# Revit family: QF_ELECTROLUXPROFESSIONAL_1LSNTN_WN6-20_E
name_source: partatom
category: Attrezzature speciali
units: mm (PartAtom-declared; Revit-internal decimal feet)

## family parameters
Basato su piano di lavoro = No
Condiviso = No
Punto di calcolo locali = No
Quota connettore circolare = Usa diametro
Sempre verticale = Sì
Taglio con vuoti quando caricato = No
Tipo di parte = Normale

## types (37) — shared parameters
Depth = 915.5 mm  [stored 3.00361 ft]
Depth Actual = 915 mm  [stored 3.00197 ft]
Height = 1346.8 mm  [stored 4.41864 ft]
Height Actual = 1345 mm
Latent Heat Output = 0.0
Length Actual = 750 mm  [stored 2.46063 ft]
Modello = WN6-20
Produttore = Electrolux Professional
Sensible Heat Output = 0.0
URL = www.electroluxprofessional.com
Weight = 207
Width = 750 mm  [stored 2.46063 ft]
zero-valued in all types: Gas KW, Prospetto di default, Steam Pounds per Hour

## per-type parameters (varying)
| type | Cycle | Descrizione | Item Number | Phase | Volts | Watts |
| 9867830144 | 50 Hz | WASHER WN6-20 20KG NO HEAT 220-240/50/1N COMPASS PRO 6G01 ML 2xWATER POWDER+5xLIQ. VALV.OPEN SILVER 2.I/O DISCON. STOP | 1L0GCA | 1 | 240 V | 800 W |
| 9867830154 | 50 Hz | WASHER WN6-20 20KG EL 13KW 220-240/50/3 COMPASS PRO 6G01 ML 2xWATER POWDER+5xLIQ. VALV.OPEN SILVER 2.I/O DISCON. STOP | 1LSP91 | 3 | 240 V | 13500 W |
| 9867830253 | 50 Hz | WASHER WN6-20 20KG NO HEAT 220-240/50/1N COMPASS PRO 6G01 ML 2xWATER POWDER VALV.OPEN SILVER DISCON. STOP | 1LSPS4 | 1 | 240 V | 800 W |
| 9867830293 | 50 Hz | WASHER WN6-20 20KG EL 13KW 380-415/50/3 COMPASS PRO 6G07 ML 2xWATER POWDER+5xLIQ. VALV.OPEN SILVER 2.I/O TRAFO DISCON. S | 1LT6KV | 3 | 415 V | 13500 W |
| 9867830266 | 60 Hz | WASHER WN6-20 20KG NO HEAT 220-240/60/1N COMPASS PRO 6L01 ML 2xWATER POWDER+5xLIQ. VALV.OPEN SILVER 2.I/O DISCON. | 1L0H63 | 1 | 240 V | 800 W |
| 9867830286 | 60 Hz | WASHER WN6-20 20KG EL 13KW 440/60/3 COMPASS PRO 6H01 ML 2xWATER POWDER+5xLIQ. VALV.OPEN SST/SILVER 2.I/O TRAFO DISCON. S | 1LM0CL | 3 | 440 V | 13700 W |
| 9867830141 | 50 Hz | WASHER WN6-20 20KG EL 13KW 380-415/50/3N COMPASS PRO 6G01 ML 2xWATER POWDER+5xLIQ. VALV.OPEN SILVER 2.I/O DISCON. STOP | 1L0GBM | 3 | 415 V | 13500 W |
| 9867830109 | 50 Hz | WASHER WN6-20 20KG EL 13KW 380-415/50/3N COMPASS PRO 6G01 ML 2xWATER POWDER+5xLIQ. VALV.OPEN SILVER 2.I/O QC DISCON. STO | 1LSP5S | 3 | 415 V | 13500 W |
| 9867830271 | 60 Hz | WASHER WN6-20 20KG EL 13KW 220-240/60/3 COMPASS PRO 6G07 ML 2xWATER POWDER+5xLIQ. VALV.OPEN SILVER 2.I/O DISCON. STOP | 1L0HBT | 3 | 240 V | 13500 W |
| 9867830176 | 60 Hz | WASHER WN6-20 20KG EL 13KW 480/60/3 COMPASS PRO 6G01 ML 2xWATER POWDER VALV.OPEN SILVER TRAFO DISCON. STOP | 1LSPC8 | 3 | 480 V | 13700 W |
| 9867830251 | 60 Hz | WASHER WN6-20 20KG EL 13KW 220-240/60/3 COMPASS PRO 6G01 ML 2xWATER POWDER VALV.OPEN SILVER DISCON. STOP | 1LSPRP | 3 | 240 V | 13500 W |
| 9867830224 | 50 Hz | WASHER WN6-20 20KG EL 13KW 380-415/220-240/50/3N/3 COMPASS PRO 6G07 ML 2xWATER POWDER+5xLIQ. VALV.OPEN SST 2.I/O QC DISC | 1LD05Z | 3 | 415 V | 13500 W |
| 9867830229 | 60 Hz | WASHER WN6-20 20KG EL 13KW 380-415/60/3N COMPASS PRO 6G01 ML 2xWATER POWDER+5xLIQ. VALV.OPEN SILVER 2.I/O DISCON. STOP | 1LSPN9 | 3 | 415 V | 13500 W |
| 9867830204 | 60 Hz | WASHER WN6-20 20KG EL 13KW 480/60/3 COMPASS PRO 6G01 ML 2xWATER POWDER+5xLIQ. VALV.OPEN SST 2.I/O TRAFO DISCON. STOP | 1L826U | 3 | 480 V | 13700 W |
| 9867830214 | 50 Hz | WASHER WN6-20 20KG EL 13KW 380-415/50/3N COMPASS PRO 6H12 ML 2xWATER POWDER+5xLIQ. VALV.OPEN SILVER SL.DRUM 2.I/O DISCON | 1LSPJD | 3 | 415 V | 13500 W |
| 9867830264 | 50 Hz | WASHER WN6-20 20KG EL 13KW 380-415/50/3 COMPASS PRO 6G01 CH-EN 2xWATER POWDER VALV.OPEN SST/SILVER TRAFO DISCON. STOP | 1LT60S | 3 | 415 V | 13500 W |
| 9867830274 | 50 Hz | WASHER WN6-20 20KG NO HEAT 200/50/60/3 COMPASS PRO 6G41 JP,EN 2xWATER POWDER+5xLIQ. VALV.OPEN SILVER SL.DRUM 2.I/O DISCO | 1L0HDG | 3 | 200 V | 800 W |
| 9867830254 | 60 Hz | WASHER WN6-20 20KG EL 13KW 220-240/60/3 COMPASS PRO 6G07 SE 2xWATER POWDER+5xLIQ. VALV.OPEN SST/SILVER 2.I/O DISCON. STO | 1LSPSD | 3 | 240 V | 13500 W |
| 9867830289 | 60 Hz | WASHER WN6-20 20KG EL 13KW 440/60/3 COMPASS PRO 6G01 ML 2xWATER POWDER VALV.OPEN SILVER TRAFO DISCON. STOP | 1LT6DG | 3 | 440 V | 13700 W |
| 9867830227 | 50 Hz | WASHER WN6-20 20KG EL 13KW 380-415/50/3N COMPASS PRO 6G01 ML 2xWATER POWDER VALV.CLOSED SILVER DISCON. STOP | 1L0H02 | 3 | 415 V | 13500 W |
| 9867830207 | 60 Hz | WASHER WN6-20 20KG EL 13KW 380-415/60/3N COMPASS PRO 6G01 ML 2xWATER POWDER VALV.OPEN SILVER DISCON. STOP | 1LA24J | 3 | 415 V | 13500 W |
| 9867830277 | 60 Hz | WASHER WN6-20 20KG NO HEAT 220/60/3 COMPASS PRO 6G01 CH-EN 2xWATER POWDER VALV.OPEN SILVER DISCON. STOP | 1L82CX | 3 | 220 V | 800 W |
| 9867830257 | 60 Hz | WASHER WN6-20 20KG EL 13KW 220-240/60/3 COMPASS PRO 6G01 ML 2xWATER POWDER VALV.OPEN SST/SILVER DISCON. STOP | 1L0H3C | 3 | 240 V | 13500 W |
| 9867830052 | 50 Hz | WASHER WN6-20 20KG EL 13KW 380-415/50/3N COMPASS PRO 6G01 ML 2xWATER POWDER VALV.OPEN SILVER DISCON. STOP | 1L8231 | 3 | 415 V | 13500 W |
| 9867830110 | 60 Hz | WASHER WN6-20 20KG EL 13KW 440/60/3 COMPASS PRO 6G01 ML 2xWATER POWDER+5xLIQ. VALV.OPEN SST/SILVER 2.I/O TRAFO DISCON. S | 1LSP5T | 3 | 440 V | 13700 W |
| 9867830118 | 50 Hz | WASHER WN6-20 20KG EL 13KW 380-415/50/3 COMPASS PRO 6G01 ML 2xWATER POWDER VALV.OPEN SST/SILVER TRAFO DISCON. STOP | 1L824G | 3 | 415 V | 13500 W |
| 9867830165 | 60 Hz | WASHER WN6-20 20KG EL 13KW 380-415/60/3 COMPASS PRO 6G07 SE 2xWATER POWDER VALV.OPEN SST/SILVER TRAFO DISCON. STOP | 1L825Y | 3 | 415 V | 13500 W |
| 9867830202 | 60 Hz | WASHER WN6-20 20KG EL 12KW 115/60/3 COMPASS PRO 6G07 ML 2xWATER POWDER+5xLIQ. VALV.OPEN SILVER 2.I/O TRAFO DISCON. STOP | 1L8268 | 3 | 115 V | 12700 W |
| 9867830262 | 60 Hz | WASHER WN6-20 20KG EL 13KW 440/60/3 COMPASS PRO 6G01 ML 2xWATER POWDER+5xLIQ. EL.VALV.OPEN SST/SILVER 2.I/O TRAFO DISCON | 1L0H55 | 3 | 440 V | 13700 W |
| 9867830051 | 60 Hz | WASHER WN6-20 20KG EL 13KW 440/60/3 COMPASS PRO 6G01 ML 2xWATER POWDER VALV.OPEN SST/SILVER TRAFO DISCON. STOP | 1L0G8S | 3 | 440 V | 13700 W |
| 9867830054 | 50 Hz | WASHER WN6-20 20KG NO HEAT 220-240/50/1N COMPASS PRO 6L01 ML 2xWATER POWDER+5xLIQ. VALV.OPEN SILVER EXT.PM. 2.I/O DISCON | 1L0G8T | 1 | 240 V | 800 W |
| 9867830117 | 60 Hz | WASHER WN6-20 20KG NO HEAT 220-240/60/3 COMPASS PRO 6L01 ML 2xWATER POWDER VALV.OPEN SILVER DISCON. | 1LSP5W | 3 | 220 V | 800 W |
| 9867830177 | 60 Hz | WASHER WN6-20 20KG EL 13KW 480/60/3 COMPASS PRO 6G01 ML 2xWATER POWDER+5xLIQ. VALV.OPEN SST/SILVER 2.I/O TRAFO DISCON. S | 1LSPCJ | 3 | 480 V | 13700 W |
| 9867830053 | 50 Hz | WASHER WN6-20 20KG EL 13KW 380-415/50/3N COMPASS PRO 6H01 ML 2xWATER POWDER+5xLIQ. VALV.OPEN SST/SILVER 2.I/O DISCON. ST | 1L8232 | 3 | 415 V | 13500 W |
| 9867830228 | 60 Hz | WASHER WN6-20 20KG EL 13KW 440/60/3 COMPASS PRO 6G07 ML 2xWATER POWDER+5xLIQ. VALV.OPEN SST/SILVER 2.I/O TRAFO DISCON. S | 1L0H0A | 3 | 440 V | 13700 W |
| 9867830268 | 60 Hz | WASHER WN6-20 20KG EL 13KW 220-240/60/3 COMPASS PRO 6G01 ML 2xWATER POWDER+5xLIQ. VALV.OPEN SILVER 2.I/O DISCON. STOP | 1L0H9Z | 3 | 240 V | 13500 W |
| 9867830258 | 50 Hz | WASHER WN6-20 20KG NO HEAT 200/50/60/3 COMPASS PRO 6L41 JP,EN 2xWATER 5xLIQ. VALV.OPEN SILVER SL.DRUM 2.I/O DISCON. | 1LT5ZP | 3 | 200 V | 800 W |

note: [stored X ft] marks values corroborated as IEEE doubles in the binary element streams (Revit-internal decimal feet)

## geometry (parser evidence)
native form markers: Sweep x4
no freeform markers — native parametric forms only
